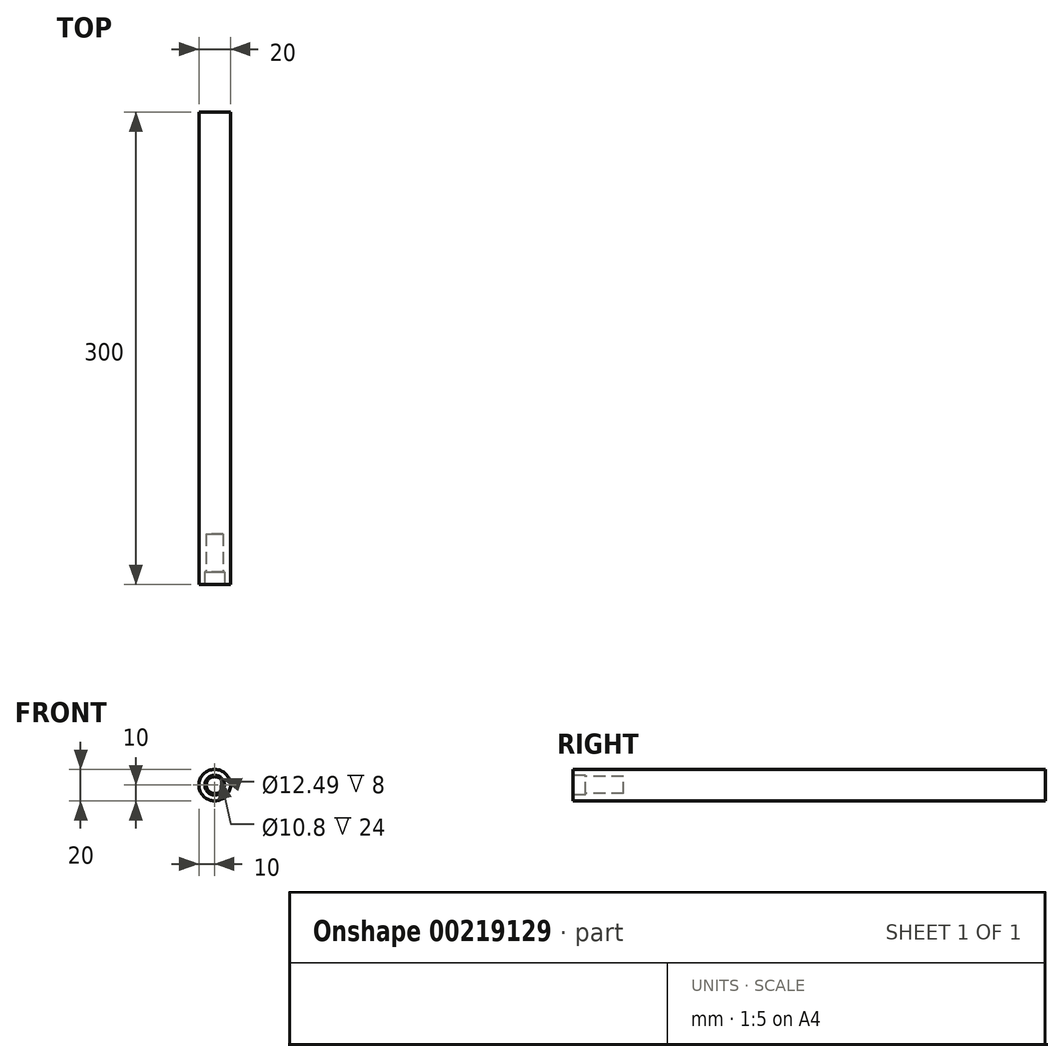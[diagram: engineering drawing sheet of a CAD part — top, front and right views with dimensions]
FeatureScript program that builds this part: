
annotation { "Feature Type Name" : "Feature", "Feature Type Description" : "" }
export const myFeature = defineFeature(function(context is Context, id is Id, definition is map)
    precondition{}
    {
        {
            var Q0;
            Q0=qCreatedBy(makeId("Front.planeOp"),FACE);
            var sketch = newSketch(context, id + "F0", { "sketchPlane" : qUnion([Q0])});
            skCircle(sketch, "E0", {"center": v(0, 0) * mm, "radius": 10 * mm});
            skSolve(sketch);
        }
        {
            var Q0;
            Q0=qSketchRegion(id+"F0",true);
            extrude(context, id + "F1", {"entities" : qUnion([Q0]), "depth" : 300 * mm});
        }
        {
            var Q0;
            Q0=makeQuery(id+"F1.opExtrude","CAP_FACE",FACE,{"disambiguationData":[OSD([sQuery(id+"F0.wireOp",EDGE,"E0")])],"isStart":false});
            var sketch = newSketch(context, id + "F2", { "sketchPlane" : qUnion([Q0])});
            skCircle(sketch, "E1", {"center": v(0, 0) * mm, "radius": 5.4 * mm});
            skSolve(sketch);
        }
        {
            var Q0;
            Q0=qSketchRegion(id+"F2",true);
            extrude(context, id + "F3", {"entities" : qUnion([Q0]), "operationType" : NewBodyOperationType.REMOVE, "oppositeDirection" : true, "depth" : 32 * mm});
        }
        {
            var Q0;
            Q0=makeQuery(id+"F1.opExtrude","CAP_FACE",FACE,{"disambiguationData":[OSD([sQuery(id+"F0.wireOp",EDGE,"E0")])],"isStart":false});
            var sketch = newSketch(context, id + "F4", { "sketchPlane" : qUnion([Q0])});
            skCircle(sketch, "E2", {"center": v(0, 0) * mm, "radius": 6.25 * mm});
            skSolve(sketch);
        }
        {
            var Q0;
            Q0=qSketchRegion(id+"F4",true);
            extrude(context, id + "F5", {"entities" : qUnion([Q0]), "operationType" : NewBodyOperationType.REMOVE, "oppositeDirection" : true, "depth" : 8 * mm});
        }
    });
